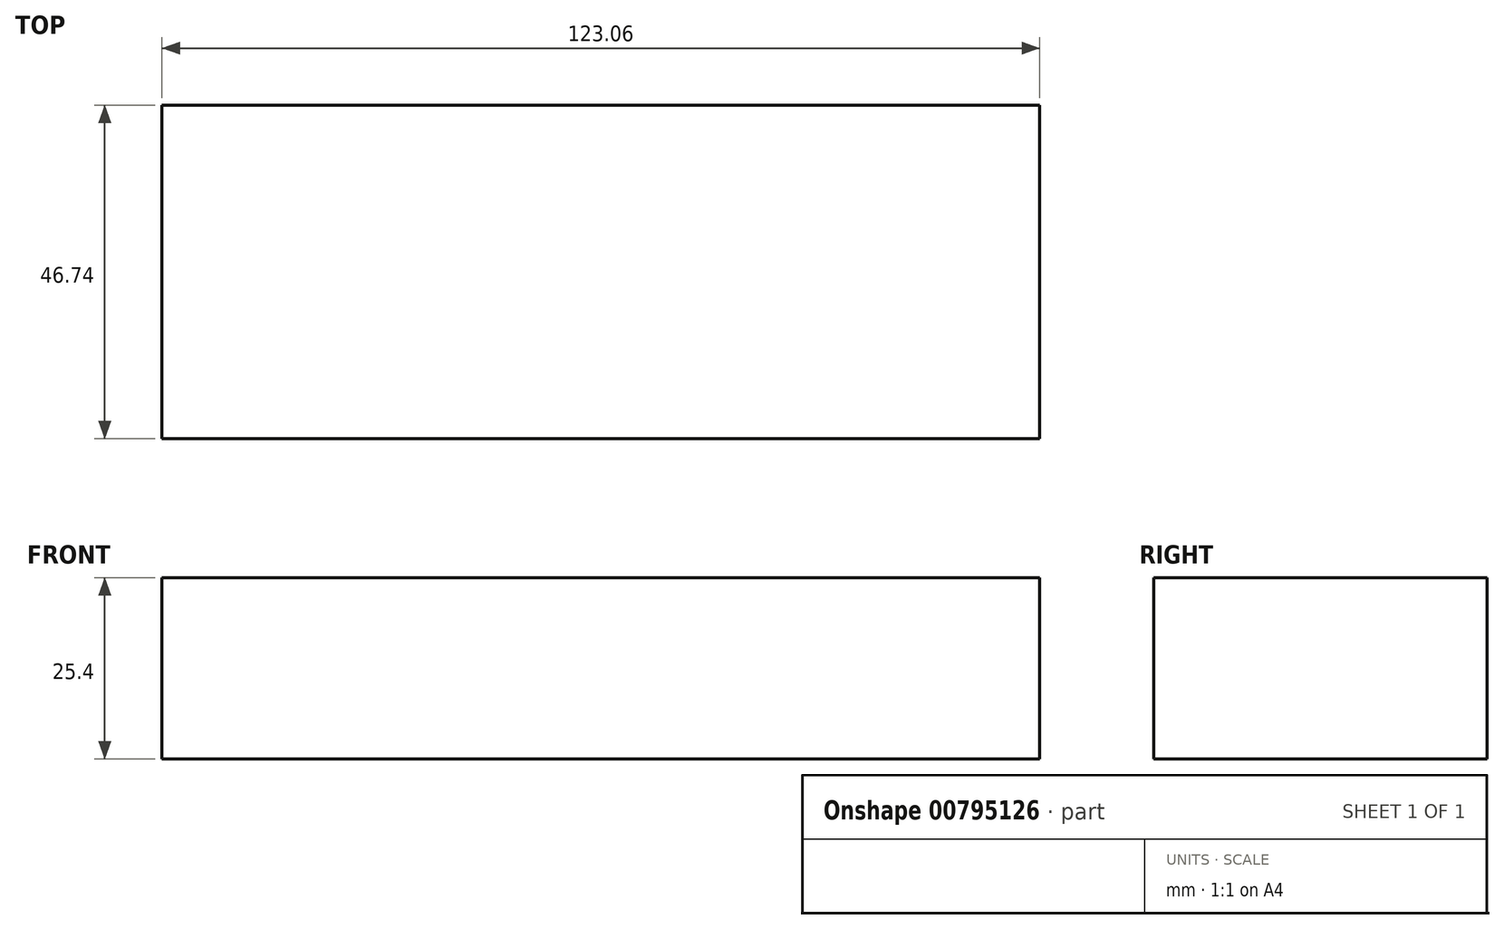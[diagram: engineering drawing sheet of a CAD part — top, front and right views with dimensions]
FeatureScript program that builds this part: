
annotation { "Feature Type Name" : "Feature", "Feature Type Description" : "" }
export const myFeature = defineFeature(function(context is Context, id is Id, definition is map)
    precondition{}
    {
        {
            var Q0;
            Q0=qCreatedBy(makeId("Top.planeOp"),FACE);
            var sketch = newSketch(context, id + "F0", { "sketchPlane" : qUnion([Q0])});
            skLineSegment(sketch, "E0.bottom", {"start": v(-61.47, 46.74) * mm, "end": v(61.59, 46.74) * mm});
            skLineSegment(sketch, "E0.top", {"start": v(-61.47, 0) * mm, "end": v(61.59, 0) * mm});
            skLineSegment(sketch, "E0.left", {"start": v(-61.47, 46.74) * mm, "end": v(-61.47, 0) * mm});
            skLineSegment(sketch, "E0.right", {"start": v(61.59, 46.74) * mm, "end": v(61.59, 0) * mm});
            skLineSegment(sketch, "E1", {"start": v(61.59, 0) * mm, "end": v(139, 48.6) * mm});
            skLineSegment(sketch, "E2", {"start": v(61.59, 46.74) * mm, "end": v(139, 48.6) * mm});
            skSolve(sketch);
        }
        {
            var Q0;
            Q0=makeQuery(id+"F0.imprint","IMPRINT",FACE,{"disambiguationData":[TD([[makeQuery(id+"F0.imprint","IMPRINT",EDGE,{"derivedFrom":sQuery(id+"F0.wireOp",EDGE,"E0.bottom")}),-1.0]])]});
            var sketch = newSketch(context, id + "F1", { "sketchPlane" : qUnion([Q0])});
            skSolve(sketch);
        }
        {
            var Q0;
            Q0=makeQuery(id+"F1.imprint","IMPRINT",FACE,{"disambiguationData":[TD([[makeQuery(id+"F1.imprint","IMPRINT",EDGE,{"derivedFrom":makeQuery(id+"F0.imprint","IMPRINT",EDGE,{"derivedFrom":sQuery(id+"F0.wireOp",EDGE,"E0.bottom")})}),-1.0]])]});
            extrude(context, id + "F2", {"entities" : qUnion([Q0]), "depth" : 25.4 * mm, "offsetDistance" : 25.4 * mm});
        }
    });
